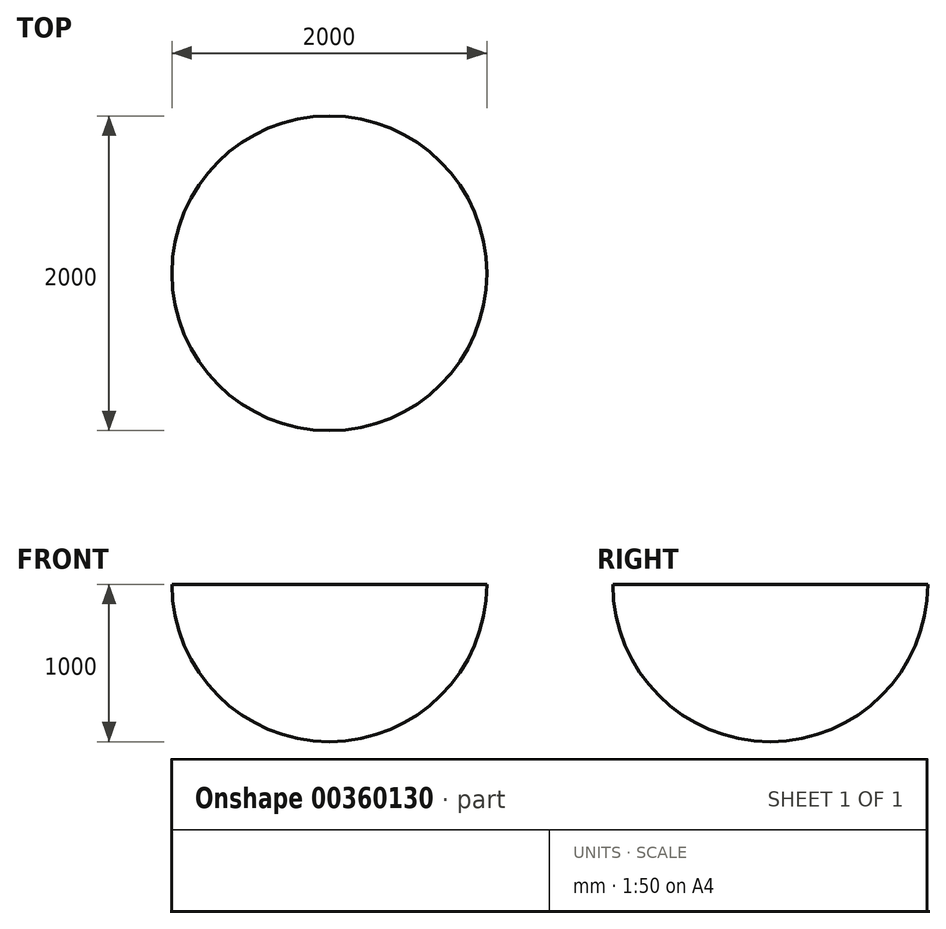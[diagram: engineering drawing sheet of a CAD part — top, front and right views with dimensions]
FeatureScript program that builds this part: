
annotation { "Feature Type Name" : "Feature", "Feature Type Description" : "" }
export const myFeature = defineFeature(function(context is Context, id is Id, definition is map)
    precondition{}
    {
        {
            var Q0;
            Q0=qCreatedBy(makeId("Top.planeOp"),FACE);
            var sketch = newSketch(context, id + "F0", { "sketchPlane" : qUnion([Q0])});
            skArc(sketch, "E0", {"start": v(1000, 0) * mm, "mid": v(0, -1000) * mm, "end": v(-1000, 0) * mm});
            skLineSegment(sketch, "E1", {"start": v(-1000, 0) * mm, "end": v(1000, 0) * mm});
            skLineSegment(sketch, "E2", {"start": v(-1000, 0) * mm, "end": v(-1000, -437.88) * mm, "construction": true});
            skLineSegment(sketch, "E3", {"start": v(1000, 0) * mm, "end": v(1000, -467.29) * mm, "construction": true});
            skSolve(sketch);
        }
        {
            var Q0;
            Q0 = qSketchRegion(id + "F0", true);
            var Q1;
            Q1=sQuery(id+"F0.wireOp",EDGE,"E1");
            revolve(context, id + "F1", {"surfaceOperationType" : NewSurfaceOperationType.NEW, "entities" : qUnion([Q0]), "axis" : qUnion([Q1]), "revolveType" : RevolveType.ONE_DIRECTION, "angle" : 180 * degree});
        }
    });
